# Revit family: Kitchen_Taps-Mixers_hansgrohe_73836XXX-Aquno-Select-M81-Single-lever-k_
name_source: partatom
category: Plumbing Fixtures
revit_build: Autodesk Revit 2015 (Build: 20140903_1530(x64)
units: mm (PartAtom-declared; Revit-internal decimal feet)

## types (3) — shared parameters
BIMobject category = Taps & Mixers
BIMobject category code = kitchen-taps
BIMobject main category = Kitchen
BIMobject main category code = kitchen
Brand url = http://www.hansgrohe-int.com
Default Elevation = 4' - 0"
Design country = Germany
Edition number = 1
GTIN code = https://4059625269442
IFC Classification = Sanitary Terminal
Installation instructions = https://www.hansgrohe.com
Manufacturer country = Germany
Manufacturer name = hansgrohe
Material main = Chrome
Product Guid = 43a4a881-0a22-4c01-a27b-c6287c46a8b2
Product SKU = 73836XXX
Product data url = https://bimobject.com
Product family = Aquno Select M81
Product group = Kitchen mixers
Product name = 73836XXX Aquno Select M81 Single lever kitchen mixer 250, pull-out spout, 2jet
Product url = https://www.hansgrohe.com
QR code = http://bimobject.com
Technical description = https://www.hansgrohe.com

## type names (no varying parameters)
- 670 Matte Black
- 800 Stainless Steel Finish
- 000 Chrome

## geometry (parser evidence)
native form markers: Sweep x3
no freeform markers — native parametric forms only
